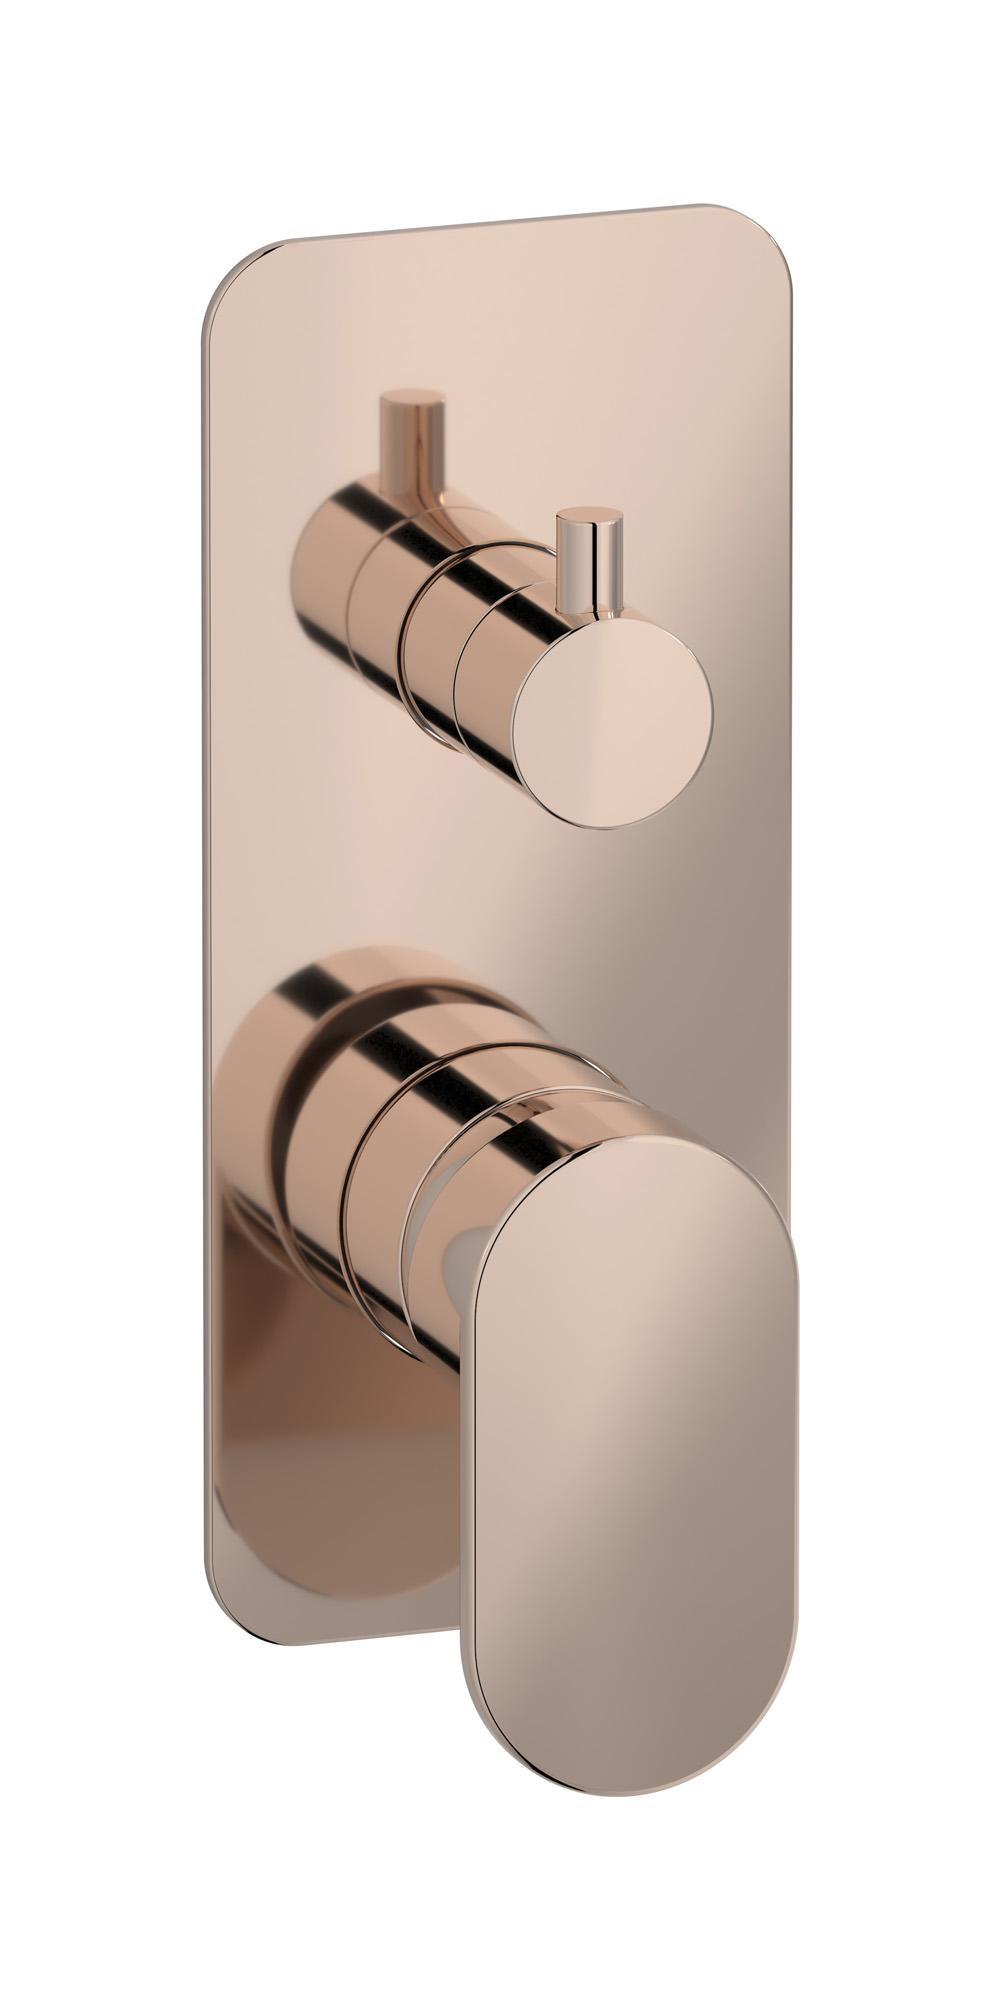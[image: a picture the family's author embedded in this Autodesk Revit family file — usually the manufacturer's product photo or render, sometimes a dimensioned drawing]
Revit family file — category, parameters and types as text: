
# Revit family: SB312
name_source: partatom
category: Apparecchi idraulici
units: mm (PartAtom-declared; Revit-internal decimal feet)

## family parameters
Basato su piano di lavoro = No
Condiviso = No
Mantieni orientamento annotazione = No
Numero OmniClass = 23.45.55.17
Punto di calcolo locali = No
Quota connettore circolare = Usa diametro
Sempre verticale = Sì
Taglio con vuoti quando caricato = No
Tipo di parte = Normale
Titolo OmniClass = Mixing Faucets

## types (6) — shared parameters
Cold water inlet = 10 mm  [stored 0.0328084 ft]
Commenti sul tipo = Wall mixer
Connessione CW = No
Connessione HW = No
Connessione di scarico = No
Connessione di ventilazione = No
Descrizione = Exposed parts for manual wall mixer with three ways diverter
Hot water inlet = 10 mm  [stored 0.0328084 ft]
Produttore = IB Rubinetterie S.p.A.
URL = https://www.weareib.it
zero-valued in all types: Prospetto di default

## per-type parameters (varying)
| type | Finishes surface | Immagine tipo | Modello |
| Chrome | IB_Chrome | SB312CC.jpg | SB312CC |
| Brushed nickel | IB_Brushed nickel | SB312SS.jpg | SB312SS |
| Natural brass | IB_Brass | SB312ON.jpg | SB312ON |
| Matt black | IB_matt black | SB312NP.jpg | SB312NP |
| Rose gold | IB_Rose gold | SB312RS.jpg | SB312RS |
| Brushed gold | IB_gold | SB312OS.jpg | SB312OS |

note: [stored X ft] marks values corroborated as IEEE doubles in the binary element streams (Revit-internal decimal feet)
